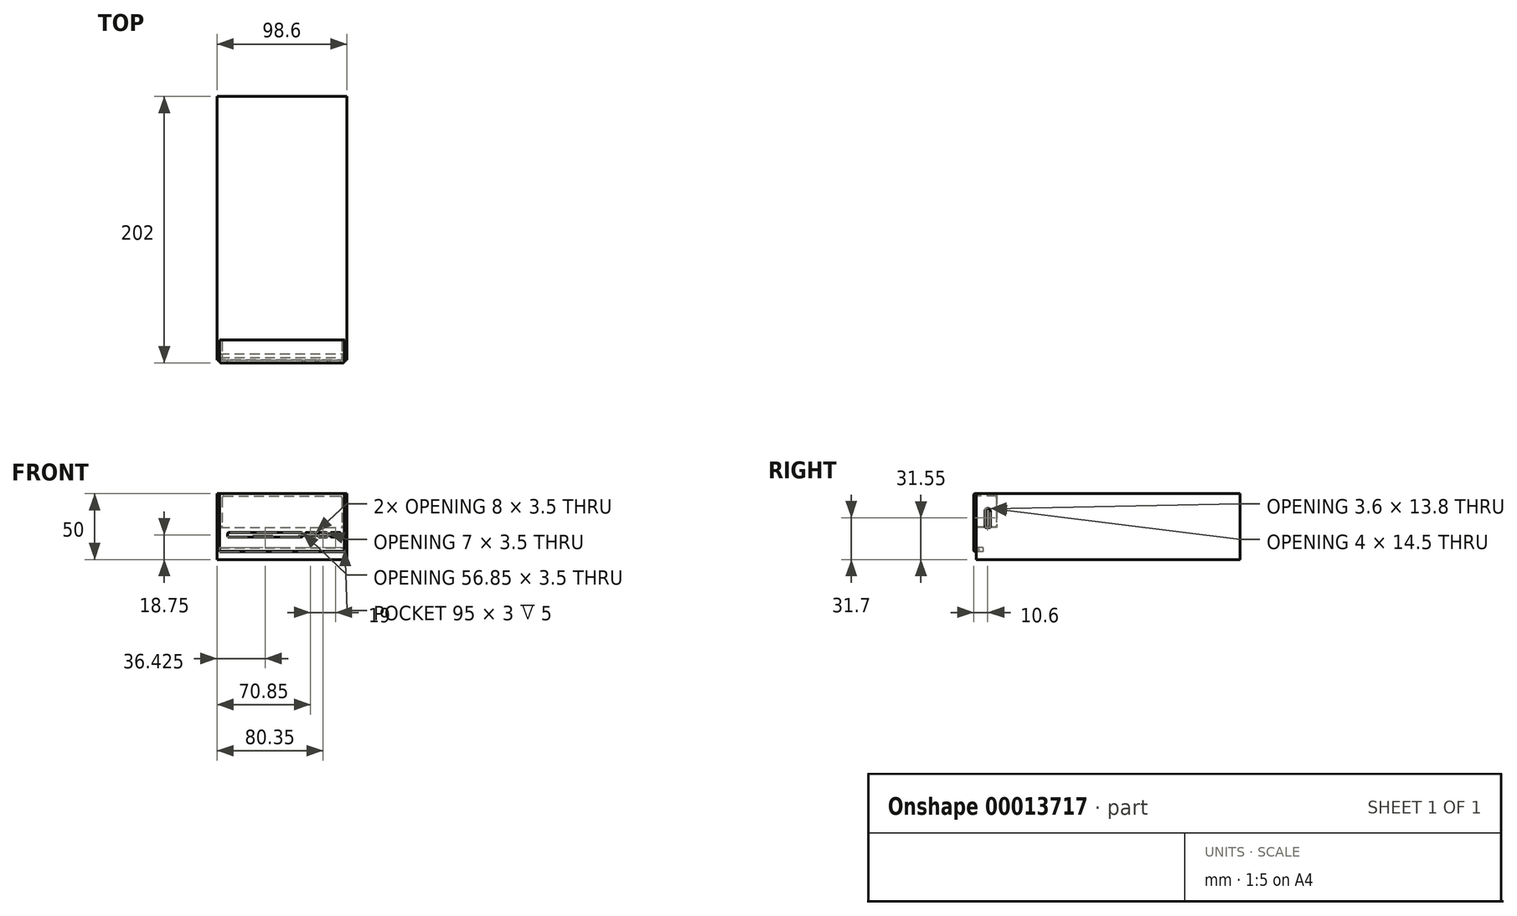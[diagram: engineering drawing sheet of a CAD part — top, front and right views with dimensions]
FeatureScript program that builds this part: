
annotation { "Feature Type Name" : "Feature", "Feature Type Description" : "" }
export const myFeature = defineFeature(function(context is Context, id is Id, definition is map)
    precondition{}
    {
        {
            var Q0;
            Q0=qCreatedBy(makeId("Front.planeOp"),FACE);
            var sketch = newSketch(context, id + "F0", { "sketchPlane" : qUnion([Q0])});
            skLineSegment(sketch, "E0.rect.bottom", {"start": v(49.3, 25) * mm, "end": v(-49.3, 25) * mm});
            skLineSegment(sketch, "E0.rect.top", {"start": v(49.3, -25) * mm, "end": v(-49.3, -25) * mm});
            skLineSegment(sketch, "E0.rect.left", {"start": v(49.3, 25) * mm, "end": v(49.3, -25) * mm});
            skLineSegment(sketch, "E0.rect.right", {"start": v(-49.3, 25) * mm, "end": v(-49.3, -25) * mm});
            skPoint(sketch, "E0.rect.middle", {"position": v(0, 0) * mm});
            skLineSegment(sketch, "E1", {"start": v(-47.5, 25) * mm, "end": v(-47.5, -25) * mm});
            skLineSegment(sketch, "E2", {"start": v(47.5, 25) * mm, "end": v(47.5, -25) * mm});
            skLineSegment(sketch, "E3", {"start": v(-49.3, 0) * mm, "end": v(-47.5, 0) * mm, "construction": true});
            skLineSegment(sketch, "E4", {"start": v(49.3, 0) * mm, "end": v(47.5, 0) * mm, "construction": true});
            skLineSegment(sketch, "E5", {"start": v(-47.5, -0.7) * mm, "end": v(47.5, -0.7) * mm});
            skLineSegment(sketch, "E6", {"start": v(44.55, -0.7) * mm, "end": v(44.55, -25) * mm, "construction": true});
            skLineSegment(sketch, "E7", {"start": v(17.3, -0.7) * mm, "end": v(17.3, -25) * mm, "construction": true});
            skLineSegment(sketch, "E8", {"start": v(-47.5, -8) * mm, "end": v(47.5, -8) * mm, "construction": true});
            skLineSegment(sketch, "E9", {"start": v(-47.5, -4.5) * mm, "end": v(47.5, -4.5) * mm, "construction": true});
            skLineSegment(sketch, "E10", {"start": v(-47.5, -19) * mm, "end": v(47.5, -19) * mm, "construction": true});
            skSolve(sketch);
        }
        {
            var Q0;
            {var subQ0=sQuery(id+"F0.wireOp",EDGE,"E5");Q0=makeQuery(id+"F0.imprint","IMPRINT",FACE,{"disambiguationData":[TD([[makeQuery(id+"F0.imprint","IMPRINT",EDGE,{"derivedFrom":subQ0}),1.0]])]});}
            var Q1;
            {var subQ6=sQuery(id+"F0.wireOp",EDGE,"E0.rect.right");Q1=makeQuery(id+"F0.imprint","IMPRINT",FACE,{"disambiguationData":[TD([[makeQuery(id+"F0.imprint","IMPRINT",EDGE,{"derivedFrom":subQ6}),1.0]])]});}
            var Q2;
            {var subQ0=sQuery(id+"F0.wireOp",EDGE,"E5");Q2=makeQuery(id+"F0.imprint","IMPRINT",FACE,{"disambiguationData":[TD([[makeQuery(id+"F0.imprint","IMPRINT",EDGE,{"derivedFrom":subQ0}),-1.0]])]});}
            var Q3;
            {var subQ6=sQuery(id+"F0.wireOp",EDGE,"E0.rect.left");Q3=makeQuery(id+"F0.imprint","IMPRINT",FACE,{"disambiguationData":[TD([[makeQuery(id+"F0.imprint","IMPRINT",EDGE,{"derivedFrom":subQ6}),-1.0]])]});}
            extrude(context, id + "F1", {"entities" : qUnion([Q0, Q1, Q2, Q3]), "oppositeDirection" : true, "depth" : 200 * mm});
        }
        {
            var Q0;
            {var subQ0=sQuery(id+"F0.wireOp",EDGE,"E5");Q0=makeQuery(id+"F0.imprint","IMPRINT",FACE,{"disambiguationData":[TD([[makeQuery(id+"F0.imprint","IMPRINT",EDGE,{"derivedFrom":subQ0}),1.0]])]});}
            extrude(context, id + "F2", {"entities" : qUnion([Q0]), "operationType" : NewBodyOperationType.REMOVE, "oppositeDirection" : true, "depth" : 15.5 * mm});
        }
        {
            var Q0;
            {var subQ0=sQuery(id+"F0.wireOp",EDGE,"E5");Q0=makeQuery(id+"F0.imprint","IMPRINT",FACE,{"disambiguationData":[TD([[makeQuery(id+"F0.imprint","IMPRINT",EDGE,{"derivedFrom":subQ0}),-1.0]])]});}
            var sketch = newSketch(context, id + "F3", { "sketchPlane" : qUnion([Q0])});
            skLineSegment(sketch, "E11.0", {"start": v(18.55, -4.5) * mm, "end": v(43.55, -4.5) * mm});
            skLineSegment(sketch, "E12.0", {"start": v(18.55, -8) * mm, "end": v(43.55, -8) * mm});
            skLineSegment(sketch, "E13.0", {"start": v(44.55, -5.5) * mm, "end": v(44.55, -7) * mm});
            skPoint(sketch, "E14.orphan", {"position": v(17.3, -0.7) * mm});
            skPoint(sketch, "E15.orphan", {"position": v(-47.5, -4.5) * mm});
            skPoint(sketch, "E16.orphan", {"position": v(-47.5, -8) * mm});
            skPoint(sketch, "E17.orphan", {"position": v(17.3, -25) * mm});
            skPoint(sketch, "E18.orphan", {"position": v(44.55, -25) * mm});
            skPoint(sketch, "E19.orphan", {"position": v(47.5, -8) * mm});
            skPoint(sketch, "E20.orphan", {"position": v(47.5, -4.5) * mm});
            skPoint(sketch, "E21.orphan", {"position": v(44.55, -0.7) * mm});
            skArc(sketch, "E22.filletArc", {"start": v(18.55, -4.5) * mm, "mid": v(17.84, -4.8) * mm, "end": v(17.55, -5.5) * mm});
            skArc(sketch, "E23.filletArc", {"start": v(17.55, -7) * mm, "mid": v(17.84, -7.7) * mm, "end": v(18.55, -8) * mm});
            skPoint(sketch, "E24.visualSharp", {"position": v(44.55, -8) * mm});
            skArc(sketch, "E24.filletArc", {"start": v(43.55, -8) * mm, "mid": v(44.26, -7.7) * mm, "end": v(44.55, -7) * mm});
            skPoint(sketch, "E25.visualSharp", {"position": v(44.55, -4.5) * mm});
            skArc(sketch, "E25.filletArc", {"start": v(44.55, -5.5) * mm, "mid": v(44.26, -4.8) * mm, "end": v(43.55, -4.5) * mm});
            skLineSegment(sketch, "E26", {"start": v(-41.3, -5.5) * mm, "end": v(-41.3, -7) * mm});
            skLineSegment(sketch, "E27", {"start": v(14.55, -8) * mm, "end": v(-40.3, -8) * mm});
            skLineSegment(sketch, "E28", {"start": v(14.55, -4.5) * mm, "end": v(-40.3, -4.5) * mm});
            skArc(sketch, "E29.filletArc", {"start": v(14.55, -8) * mm, "mid": v(15.26, -7.7) * mm, "end": v(15.55, -7) * mm});
            skArc(sketch, "E30.filletArc", {"start": v(15.55, -5.5) * mm, "mid": v(15.26, -4.8) * mm, "end": v(14.55, -4.5) * mm});
            skPoint(sketch, "E31.visualSharp", {"position": v(-41.3, -8) * mm});
            skArc(sketch, "E31.filletArc", {"start": v(-41.3, -7) * mm, "mid": v(-41, -7.7) * mm, "end": v(-40.3, -8) * mm});
            skPoint(sketch, "E32.visualSharp", {"position": v(-41.3, -4.5) * mm});
            skArc(sketch, "E32.filletArc", {"start": v(-40.3, -4.5) * mm, "mid": v(-41, -4.8) * mm, "end": v(-41.3, -5.5) * mm});
            skLineSegment(sketch, "E33", {"start": v(15.55, -5.5) * mm, "end": v(15.55, -7) * mm});
            skLineSegment(sketch, "E34", {"start": v(17.55, -5.5) * mm, "end": v(17.55, -7) * mm});
            skLineSegment(sketch, "E35", {"start": v(25.55, -4.5) * mm, "end": v(25.55, -8) * mm});
            skLineSegment(sketch, "E36", {"start": v(36.55, -4.5) * mm, "end": v(36.55, -8) * mm});
            skLineSegment(sketch, "E37", {"start": v(27.55, -4.5) * mm, "end": v(27.55, -8) * mm});
            skLineSegment(sketch, "E38", {"start": v(34.55, -4.5) * mm, "end": v(34.55, -8) * mm});
            skLineSegment(sketch, "E39", {"start": v(-49.3, -16) * mm, "end": v(49.3, -16) * mm});
            skLineSegment(sketch, "E40.0", {"start": v(-49.3, 25) * mm, "end": v(-49.3, -25) * mm});
            skLineSegment(sketch, "E41.0", {"start": v(49.3, 25) * mm, "end": v(49.3, -25) * mm});
            skLineSegment(sketch, "E42.0", {"start": v(-47.5, -19) * mm, "end": v(47.5, -19) * mm});
            skLineSegment(sketch, "E43", {"start": v(-47.5, -19) * mm, "end": v(-47.5, -16) * mm});
            skLineSegment(sketch, "E44", {"start": v(47.5, -19) * mm, "end": v(47.5, -16) * mm});
            skSolve(sketch);
        }
        {
            var Q0;
            Q0=makeQuery(id+"F1.opExtrude","SWEPT_FACE",FACE,{"disambiguationData":[OSD([sQuery(id+"F0.wireOp",EDGE,"E0.rect.right")])]});
            var sketch = newSketch(context, id + "F4", { "sketchPlane" : qUnion([Q0])});
            skLineSegment(sketch, "E45", {"start": v(-6.6, 11.8) * mm, "end": v(-6.6, -0.7) * mm});
            skLineSegment(sketch, "E46", {"start": v(-10.6, 11.8) * mm, "end": v(-10.6, -0.7) * mm});
            skLineSegment(sketch, "E47", {"start": v(-8.6, 13.8) * mm, "end": v(-8.6, 13.8) * mm});
            skLineSegment(sketch, "E48.0", {"start": v(-10.6, -0.7) * mm, "end": v(-6.6, -0.7) * mm});
            skPoint(sketch, "E49.orphan", {"position": v(0, -0.7) * mm});
            skPoint(sketch, "E50.orphan", {"position": v(-15.5, -0.7) * mm});
            skPoint(sketch, "E51.visualSharp", {"position": v(-10.6, 13.8) * mm});
            skArc(sketch, "E51.filletArc", {"start": v(-8.6, 13.8) * mm, "mid": v(-10.01, 13.21) * mm, "end": v(-10.6, 11.8) * mm});
            skPoint(sketch, "E52.visualSharp", {"position": v(-6.6, 13.8) * mm});
            skArc(sketch, "E52.filletArc", {"start": v(-6.6, 11.8) * mm, "mid": v(-7.19, 13.21) * mm, "end": v(-8.6, 13.8) * mm});
            skSolve(sketch);
        }
        {
            var Q0;
            Q0=makeQuery(id+"F4.imprint","IMPRINT",FACE,{"disambiguationData":[TD([[makeQuery(id+"F4.imprint","IMPRINT",EDGE,{"derivedFrom":sQuery(id+"F4.wireOp",EDGE,"E45")}),-1.0]])]});
            extrude(context, id + "F5", {"entities" : qUnion([Q0]), "operationType" : NewBodyOperationType.REMOVE, "endBound" : BoundingType.THROUGH_ALL, "oppositeDirection" : true, "depth" : 133.9 * mm});
        }
        {
            var Q0;
            Q0=makeQuery(id+"F3.imprint","IMPRINT",FACE,{"disambiguationData":[TD([[makeQuery(id+"F3.imprint","IMPRINT",EDGE,{"derivedFrom":sQuery(id+"F3.wireOp",EDGE,"E42.0")}),1.0]])]});
            extrude(context, id + "F6", {"entities" : qUnion([Q0]), "operationType" : NewBodyOperationType.REMOVE, "oppositeDirection" : true, "depth" : 5 * mm});
        }
        {
            var Q0;
            {var subQ0=sQuery(id+"F0.wireOp",EDGE,"E5");Q0=makeQuery(id+"F0.imprint","IMPRINT",FACE,{"disambiguationData":[TD([[makeQuery(id+"F0.imprint","IMPRINT",EDGE,{"derivedFrom":subQ0}),-1.0]])]});}
            var sketch = newSketch(context, id + "F7", { "sketchPlane" : qUnion([Q0])});
            skArc(sketch, "E53.0.0", {"start": v(-40.3, -4.5) * mm, "mid": v(-41, -4.8) * mm, "end": v(-41.3, -5.5) * mm});
            skLineSegment(sketch, "E53.0.1", {"start": v(-41.3, -5.5) * mm, "end": v(-41.3, -7) * mm});
            skArc(sketch, "E53.0.2", {"start": v(-41.3, -7) * mm, "mid": v(-41, -7.7) * mm, "end": v(-40.3, -8) * mm});
            skLineSegment(sketch, "E53.0.3", {"start": v(14.55, -8) * mm, "end": v(-40.3, -8) * mm});
            skArc(sketch, "E53.0.4", {"start": v(14.55, -8) * mm, "mid": v(15.26, -7.7) * mm, "end": v(15.55, -7) * mm});
            skLineSegment(sketch, "E53.0.5", {"start": v(15.55, -5.5) * mm, "end": v(15.55, -7) * mm});
            skArc(sketch, "E53.0.6", {"start": v(15.55, -5.5) * mm, "mid": v(15.26, -4.8) * mm, "end": v(14.55, -4.5) * mm});
            skLineSegment(sketch, "E53.0.7", {"start": v(14.55, -4.5) * mm, "end": v(-40.3, -4.5) * mm});
            skLineSegment(sketch, "E54.0.0", {"start": v(18.55, -4.5) * mm, "end": v(25.55, -4.5) * mm});
            skArc(sketch, "E54.0.1", {"start": v(18.55, -4.5) * mm, "mid": v(17.84, -4.8) * mm, "end": v(17.55, -5.5) * mm});
            skLineSegment(sketch, "E54.0.2", {"start": v(17.55, -5.5) * mm, "end": v(17.55, -7) * mm});
            skArc(sketch, "E54.0.3", {"start": v(17.55, -7) * mm, "mid": v(17.84, -7.7) * mm, "end": v(18.55, -8) * mm});
            skLineSegment(sketch, "E54.0.4", {"start": v(18.55, -8) * mm, "end": v(25.55, -8) * mm});
            skLineSegment(sketch, "E54.0.5", {"start": v(25.55, -4.5) * mm, "end": v(25.55, -8) * mm});
            skLineSegment(sketch, "E55.0.0", {"start": v(27.55, -4.5) * mm, "end": v(34.55, -4.5) * mm});
            skLineSegment(sketch, "E55.0.1", {"start": v(27.55, -4.5) * mm, "end": v(27.55, -8) * mm});
            skLineSegment(sketch, "E55.0.2", {"start": v(27.55, -8) * mm, "end": v(34.55, -8) * mm});
            skLineSegment(sketch, "E55.0.3", {"start": v(34.55, -4.5) * mm, "end": v(34.55, -8) * mm});
            skLineSegment(sketch, "E56.0.0", {"start": v(36.55, -4.5) * mm, "end": v(43.55, -4.5) * mm});
            skLineSegment(sketch, "E56.0.1", {"start": v(36.55, -4.5) * mm, "end": v(36.55, -8) * mm});
            skLineSegment(sketch, "E56.0.2", {"start": v(36.55, -8) * mm, "end": v(43.55, -8) * mm});
            skArc(sketch, "E56.0.3", {"start": v(43.55, -8) * mm, "mid": v(44.26, -7.7) * mm, "end": v(44.55, -7) * mm});
            skLineSegment(sketch, "E56.0.4", {"start": v(44.55, -5.5) * mm, "end": v(44.55, -7) * mm});
            skArc(sketch, "E56.0.5", {"start": v(44.55, -5.5) * mm, "mid": v(44.26, -4.8) * mm, "end": v(43.55, -4.5) * mm});
            skLineSegment(sketch, "E57.0", {"start": v(-47.5, 25) * mm, "end": v(-47.5, -25) * mm, "construction": true});
            skLineSegment(sketch, "E58.0", {"start": v(47.5, 25) * mm, "end": v(47.5, -25) * mm, "construction": true});
            skLineSegment(sketch, "E59.0", {"start": v(-47.5, -19) * mm, "end": v(47.5, -19) * mm, "construction": true});
            skLineSegment(sketch, "E60.0", {"start": v(-49.3, -16) * mm, "end": v(49.3, -16) * mm, "construction": true});
            skLineSegment(sketch, "E61.0", {"start": v(-47.5, -0.7) * mm, "end": v(47.5, -0.7) * mm, "construction": true});
            skLineSegment(sketch, "E62", {"start": v(-47.3, 25) * mm, "end": v(-47.3, -31.56) * mm});
            skLineSegment(sketch, "E63", {"start": v(47.3, 25) * mm, "end": v(47.3, -30.5) * mm});
            skLineSegment(sketch, "E64", {"start": v(-47.3, 25) * mm, "end": v(47.3, 25) * mm});
            skLineSegment(sketch, "E65", {"start": v(-45.3, -0.4) * mm, "end": v(45.3, -0.4) * mm});
            skLineSegment(sketch, "E66", {"start": v(-47.3, -16.2) * mm, "end": v(47.3, -16.2) * mm});
            skLineSegment(sketch, "E67", {"start": v(47.3, -18.8) * mm, "end": v(-47.3, -18.8) * mm});
            skLineSegment(sketch, "E68", {"start": v(-45.3, 23) * mm, "end": v(45.3, 23) * mm});
            skLineSegment(sketch, "E69", {"start": v(-45.3, 23) * mm, "end": v(-45.3, -0.4) * mm});
            skLineSegment(sketch, "E70", {"start": v(45.3, 23) * mm, "end": v(45.3, -0.4) * mm});
            skLineSegment(sketch, "E71", {"start": v(-45.3, 1.6) * mm, "end": v(45.3, 1.6) * mm});
            skLineSegment(sketch, "E72", {"start": v(-45.3, -0.4) * mm, "end": v(-47.3, -0.4) * mm});
            skLineSegment(sketch, "E73", {"start": v(45.3, -0.4) * mm, "end": v(47.3, -0.4) * mm});
            skSolve(sketch);
        }
        {
            var Q0;
            {var subQ9=sQuery(id+"F7.wireOp",EDGE,"E64");Q0=makeQuery(id+"F7.imprint","IMPRINT",FACE,{"disambiguationData":[TD([[makeQuery(id+"F7.imprint","IMPRINT",EDGE,{"derivedFrom":subQ9}),-1.0]])]});}
            var Q1;
            {var subQ2=sQuery(id+"F7.wireOp",EDGE,"E65");Q1=makeQuery(id+"F7.imprint","IMPRINT",FACE,{"disambiguationData":[TD([[makeQuery(id+"F7.imprint","IMPRINT",EDGE,{"derivedFrom":subQ2}),1.0]])]});}
            var Q2;
            {var subQ2=sQuery(id+"F7.wireOp",EDGE,"E68");Q2=makeQuery(id+"F7.imprint","IMPRINT",FACE,{"disambiguationData":[TD([[makeQuery(id+"F7.imprint","IMPRINT",EDGE,{"derivedFrom":subQ2}),-1.0]])]});}
            var Q3;
            Q3=makeQuery(id+"F7.imprint","IMPRINT",FACE,{"disambiguationData":[TD([[makeQuery(id+"F7.imprint","IMPRINT",EDGE,{"derivedFrom":sQuery(id+"F7.wireOp",EDGE,"E65")}),-1.0]])]});
            var Q4;
            Q4=makeQuery(id+"F7.imprint","IMPRINT",FACE,{"disambiguationData":[TD([[makeQuery(id+"F7.imprint","IMPRINT",EDGE,{"derivedFrom":sQuery(id+"F7.wireOp",EDGE,"E53.0.0")}),-1.0]])]});
            var Q5;
            {var subQ1=sQuery(id+"F7.wireOp",EDGE,"E66");Q5=makeQuery(id+"F7.imprint","IMPRINT",FACE,{"disambiguationData":[TD([[makeQuery(id+"F7.imprint","IMPRINT",EDGE,{"derivedFrom":subQ1}),-1.0]])]});}
            extrude(context, id + "F8", {"entities" : qUnion([Q0, Q1, Q2, Q3, Q4, Q5]), "depth" : 2 * mm});
        }
        {
            var Q0;
            {var subQ9=sQuery(id+"F7.wireOp",EDGE,"E64");Q0=makeQuery(id+"F7.imprint","IMPRINT",FACE,{"disambiguationData":[TD([[makeQuery(id+"F7.imprint","IMPRINT",EDGE,{"derivedFrom":subQ9}),-1.0]])]});}
            extrude(context, id + "F9", {"entities" : qUnion([Q0]), "operationType" : NewBodyOperationType.ADD, "oppositeDirection" : true, "depth" : 15.3 * mm});
        }
        {
            var Q0;
            {var subQ1=sQuery(id+"F7.wireOp",EDGE,"E66");Q0=makeQuery(id+"F7.imprint","IMPRINT",FACE,{"disambiguationData":[TD([[makeQuery(id+"F7.imprint","IMPRINT",EDGE,{"derivedFrom":subQ1}),-1.0]])]});}
            extrude(context, id + "F10", {"entities" : qUnion([Q0]), "operationType" : NewBodyOperationType.ADD, "oppositeDirection" : true, "depth" : 2 * mm});
        }
        {
            var Q0;
            {var subQ0=sQuery(id+"F7.wireOp",EDGE,"E62");Q0=makeQuery(id+"F10.boolean.opBoolean","MERGE",FACE,{"derivedFrom":[makeQuery(id+"F9.boolean.opBoolean","MERGE",FACE,{"derivedFrom":[makeQuery(id+"F8.opExtrude","SWEPT_FACE",FACE,{"disambiguationData":[OSD([subQ0])]}),makeQuery(id+"F9.opExtrude","SWEPT_FACE",FACE,{"disambiguationData":[OSD([subQ0])]})]}),makeQuery(id+"F10.opExtrude","SWEPT_FACE",FACE,{"disambiguationData":[OSD([subQ0])]})]});}
            var sketch = newSketch(context, id + "F11", { "sketchPlane" : qUnion([Q0])});
            skLineSegment(sketch, "E74.0", {"start": v(-6.6, 11.8) * mm, "end": v(-6.6, -0.4) * mm});
            skArc(sketch, "E75.0", {"start": v(-6.6, 11.8) * mm, "mid": v(-8.6, 13.8) * mm, "end": v(-10.6, 11.8) * mm});
            skLineSegment(sketch, "E76.0", {"start": v(-10.6, 11.8) * mm, "end": v(-10.6, -0.4) * mm});
            skLineSegment(sketch, "E77.0", {"start": v(-10.6, -0.4) * mm, "end": v(-6.6, -0.4) * mm});
            skPoint(sketch, "E78.orphan", {"position": v(-6.6, -0.7) * mm});
            skPoint(sketch, "E79.orphan", {"position": v(-10.6, -0.7) * mm});
            skPoint(sketch, "E80.orphan", {"position": v(0, -0.4) * mm});
            skPoint(sketch, "E81.orphan", {"position": v(-15.3, -0.4) * mm});
            skLineSegment(sketch, "E82.0", {"start": v(-6.8, 11.8) * mm, "end": v(-6.8, -0.2) * mm});
            skArc(sketch, "E82.1", {"start": v(-6.8, 11.8) * mm, "mid": v(-8.6, 13.6) * mm, "end": v(-10.4, 11.8) * mm});
            skLineSegment(sketch, "E82.2", {"start": v(-10.4, 11.8) * mm, "end": v(-10.4, -0.2) * mm});
            skLineSegment(sketch, "E82.3", {"start": v(-10.4, -0.2) * mm, "end": v(-6.8, -0.2) * mm});
            skSolve(sketch);
        }
        {
            var Q0;
            Q0=makeQuery(id+"F11.imprint","IMPRINT",FACE,{"disambiguationData":[TD([[makeQuery(id+"F11.imprint","IMPRINT",EDGE,{"derivedFrom":sQuery(id+"F11.wireOp",EDGE,"E82.0")}),-1.0]])]});
            extrude(context, id + "F12", {"entities" : qUnion([Q0]), "operationType" : NewBodyOperationType.ADD, "depth" : 1 * mm});
        }
        {
            var Q0;
            {var subQ0=sQuery(id+"F7.wireOp",EDGE,"E63");Q0=makeQuery(id+"F10.boolean.opBoolean","MERGE",FACE,{"derivedFrom":[makeQuery(id+"F9.boolean.opBoolean","MERGE",FACE,{"derivedFrom":[makeQuery(id+"F8.opExtrude","SWEPT_FACE",FACE,{"disambiguationData":[OSD([subQ0])]}),makeQuery(id+"F9.opExtrude","SWEPT_FACE",FACE,{"disambiguationData":[OSD([subQ0])]})]}),makeQuery(id+"F10.opExtrude","SWEPT_FACE",FACE,{"disambiguationData":[OSD([subQ0])]})]});}
            var sketch = newSketch(context, id + "F13", { "sketchPlane" : qUnion([Q0])});
            skLineSegment(sketch, "E83.0.0", {"start": v(6.8, 11.8) * mm, "end": v(6.8, -0.2) * mm});
            skArc(sketch, "E83.0.1", {"start": v(6.8, 11.8) * mm, "mid": v(8.6, 13.6) * mm, "end": v(10.4, 11.8) * mm});
            skLineSegment(sketch, "E83.0.2", {"start": v(10.4, 11.8) * mm, "end": v(10.4, -0.2) * mm});
            skLineSegment(sketch, "E83.0.3", {"start": v(10.4, -0.2) * mm, "end": v(6.8, -0.2) * mm});
            skSolve(sketch);
        }
        {
            var Q0;
            Q0=makeQuery(id+"F13.imprint","IMPRINT",FACE,{"disambiguationData":[TD([[makeQuery(id+"F13.imprint","IMPRINT",EDGE,{"derivedFrom":sQuery(id+"F13.wireOp",EDGE,"E83.0.0")}),1.0]])]});
            extrude(context, id + "F14", {"entities" : qUnion([Q0]), "operationType" : NewBodyOperationType.ADD, "depth" : 1 * mm});
        }
        {
            var Q0;
            Q0=makeQuery(id+"F14.opExtrude","CAP_EDGE",EDGE,{"disambiguationData":[OSD([sQuery(id+"F13.wireOp",EDGE,"E83.0.2")])],"isStart":false});
            var Q1;
            Q1=makeQuery(id+"F14.opExtrude","CAP_EDGE",EDGE,{"disambiguationData":[OSD([sQuery(id+"F13.wireOp",EDGE,"E83.0.2")])],"isStart":true});
            var Q2;
            Q2=makeQuery(id+"F12.opExtrude","CAP_EDGE",EDGE,{"disambiguationData":[OSD([sQuery(id+"F11.wireOp",EDGE,"E82.2")])],"isStart":true});
            var Q3;
            Q3=makeQuery(id+"F12.opExtrude","CAP_EDGE",EDGE,{"disambiguationData":[OSD([sQuery(id+"F11.wireOp",EDGE,"E82.2")])],"isStart":false});
            var Q4;
            Q4=makeQuery(id+"F14.opExtrude","CAP_EDGE",EDGE,{"disambiguationData":[OSD([sQuery(id+"F13.wireOp",EDGE,"E83.0.3")])],"isStart":false});
            var Q5;
            Q5=makeQuery(id+"F12.opExtrude","CAP_EDGE",EDGE,{"disambiguationData":[OSD([sQuery(id+"F11.wireOp",EDGE,"E82.3")])],"isStart":false});
            fillet(context, id + "F15", {"entities" : qUnion([Q0, Q1, Q2, Q3, Q4, Q5]), "radius" : 0.5 * mm, "tangentPropagation" : true, "allowEdgeOverflow" : false});
        }
        {
            var Q0;
            Q0=makeQuery(id+"F8.opExtrude","SWEPT_EDGE",EDGE,{"disambiguationData":[OSD([sQuery(id+"F7.wireOp",EDGE,"E54.0.0"),sQuery(id+"F7.wireOp",EDGE,"E54.0.5")])]});
            var Q1;
            Q1=makeQuery(id+"F8.opExtrude","SWEPT_EDGE",EDGE,{"disambiguationData":[OSD([sQuery(id+"F7.wireOp",EDGE,"E54.0.4"),sQuery(id+"F7.wireOp",EDGE,"E54.0.5")])]});
            var Q2;
            Q2=makeQuery(id+"F8.opExtrude","SWEPT_EDGE",EDGE,{"disambiguationData":[OSD([sQuery(id+"F7.wireOp",EDGE,"E55.0.1"),sQuery(id+"F7.wireOp",EDGE,"E55.0.2")])]});
            var Q3;
            Q3=makeQuery(id+"F8.opExtrude","SWEPT_EDGE",EDGE,{"disambiguationData":[OSD([sQuery(id+"F7.wireOp",EDGE,"E55.0.0"),sQuery(id+"F7.wireOp",EDGE,"E55.0.1")])]});
            var Q4;
            Q4=makeQuery(id+"F8.opExtrude","SWEPT_EDGE",EDGE,{"disambiguationData":[OSD([sQuery(id+"F7.wireOp",EDGE,"E55.0.0"),sQuery(id+"F7.wireOp",EDGE,"E55.0.3")])]});
            var Q5;
            Q5=makeQuery(id+"F8.opExtrude","SWEPT_EDGE",EDGE,{"disambiguationData":[OSD([sQuery(id+"F7.wireOp",EDGE,"E55.0.2"),sQuery(id+"F7.wireOp",EDGE,"E55.0.3")])]});
            var Q6;
            Q6=makeQuery(id+"F8.opExtrude","SWEPT_EDGE",EDGE,{"disambiguationData":[OSD([sQuery(id+"F7.wireOp",EDGE,"E56.0.1"),sQuery(id+"F7.wireOp",EDGE,"E56.0.2")])]});
            var Q7;
            Q7=makeQuery(id+"F8.opExtrude","SWEPT_EDGE",EDGE,{"disambiguationData":[OSD([sQuery(id+"F7.wireOp",EDGE,"E56.0.0"),sQuery(id+"F7.wireOp",EDGE,"E56.0.1")])]});
            fillet(context, id + "F16", {"entities" : qUnion([Q0, Q1, Q2, Q3, Q4, Q5, Q6, Q7]), "radius" : 1 * mm, "tangentPropagation" : true, "allowEdgeOverflow" : false});
        }
        {
            var Q0;
            Q0=makeQuery(id+"F8.opExtrude","CAP_EDGE",EDGE,{"disambiguationData":[OSD([sQuery(id+"F7.wireOp",EDGE,"E64")])],"isStart":false});
            var Q1;
            Q1=makeQuery(id+"F9.opExtrude","CAP_EDGE",EDGE,{"disambiguationData":[OSD([sQuery(id+"F7.wireOp",EDGE,"E64")])],"isStart":false});
            var Q2;
            {var subQ0=sQuery(id+"F7.wireOp",EDGE,"E62");var subQ1=sQuery(id+"F7.wireOp",EDGE,"E64");Q2=makeQuery(id+"F9.boolean.opBoolean","MERGE",EDGE,{"derivedFrom":[makeQuery(id+"F8.opExtrude","SWEPT_EDGE",EDGE,{"disambiguationData":[OSD([subQ0,subQ1])]}),makeQuery(id+"F9.opExtrude","SWEPT_EDGE",EDGE,{"disambiguationData":[OSD([subQ0,subQ1])]})]});}
            var Q3;
            {var subQ0=sQuery(id+"F7.wireOp",EDGE,"E63");var subQ1=sQuery(id+"F7.wireOp",EDGE,"E64");Q3=makeQuery(id+"F9.boolean.opBoolean","MERGE",EDGE,{"derivedFrom":[makeQuery(id+"F8.opExtrude","SWEPT_EDGE",EDGE,{"disambiguationData":[OSD([subQ0,subQ1])]}),makeQuery(id+"F9.opExtrude","SWEPT_EDGE",EDGE,{"disambiguationData":[OSD([subQ0,subQ1])]})]});}
            var Q4;
            Q4=makeQuery(id+"F9.opExtrude","CAP_EDGE",EDGE,{"disambiguationData":[OSD([sQuery(id+"F7.wireOp",EDGE,"E63")])],"isStart":false});
            var Q5;
            Q5=makeQuery(id+"F9.opExtrude","CAP_EDGE",EDGE,{"disambiguationData":[OSD([sQuery(id+"F7.wireOp",EDGE,"E62")])],"isStart":false});
            var Q6;
            Q6=makeQuery(id+"F8.opExtrude","CAP_EDGE",EDGE,{"disambiguationData":[OSD([sQuery(id+"F7.wireOp",EDGE,"E62")])],"isStart":false});
            var Q7;
            Q7=makeQuery(id+"F8.opExtrude","CAP_EDGE",EDGE,{"disambiguationData":[OSD([sQuery(id+"F7.wireOp",EDGE,"E63")])],"isStart":false});
            var Q8;
            Q8=makeQuery(id+"F8.opExtrude","CAP_EDGE",EDGE,{"disambiguationData":[OSD([sQuery(id+"F7.wireOp",EDGE,"E67")])],"isStart":false});
            var Q9;
            Q9=makeQuery(id+"F10.opExtrude","CAP_EDGE",EDGE,{"disambiguationData":[OSD([sQuery(id+"F7.wireOp",EDGE,"E67")])],"isStart":false});
            var Q10;
            Q10=makeQuery(id+"F10.opExtrude","CAP_EDGE",EDGE,{"disambiguationData":[OSD([sQuery(id+"F7.wireOp",EDGE,"E66")])],"isStart":false});
            var Q11;
            Q11=makeQuery(id+"F10.opExtrude","CAP_EDGE",EDGE,{"disambiguationData":[OSD([sQuery(id+"F7.wireOp",EDGE,"E66")])],"isStart":true});
            var Q12;
            Q12=makeQuery(id+"F9.opExtrude","CAP_EDGE",EDGE,{"disambiguationData":[OSD([sQuery(id+"F7.wireOp",EDGE,"E72")])],"isStart":false});
            var Q13;
            Q13=makeQuery(id+"F9.opExtrude","CAP_EDGE",EDGE,{"disambiguationData":[OSD([sQuery(id+"F7.wireOp",EDGE,"E73")])],"isStart":false});
            var Q14;
            Q14=makeQuery(id+"F9.opExtrude","CAP_EDGE",EDGE,{"disambiguationData":[OSD([sQuery(id+"F7.wireOp",EDGE,"E70")])],"isStart":true});
            var Q15;
            Q15=makeQuery(id+"F9.opExtrude","CAP_EDGE",EDGE,{"disambiguationData":[OSD([sQuery(id+"F7.wireOp",EDGE,"E68")])],"isStart":true});
            var Q16;
            Q16=makeQuery(id+"F9.opExtrude","CAP_EDGE",EDGE,{"disambiguationData":[OSD([sQuery(id+"F7.wireOp",EDGE,"E69")])],"isStart":true});
            var Q17;
            Q17=makeQuery(id+"F9.opExtrude","SWEPT_EDGE",EDGE,{"disambiguationData":[OSD([sQuery(id+"F7.wireOp",EDGE,"E68"),sQuery(id+"F7.wireOp",EDGE,"E69")])]});
            var Q18;
            Q18=makeQuery(id+"F9.opExtrude","SWEPT_EDGE",EDGE,{"disambiguationData":[OSD([sQuery(id+"F7.wireOp",EDGE,"E68"),sQuery(id+"F7.wireOp",EDGE,"E70")])]});
            fillet(context, id + "F17", {"entities" : qUnion([Q0, Q1, Q2, Q3, Q4, Q5, Q6, Q7, Q8, Q9, Q10, Q11, Q12, Q13, Q14, Q15, Q16, Q17, Q18]), "radius" : 1 * mm, "tangentPropagation" : true, "allowEdgeOverflow" : false});
        }
    });
